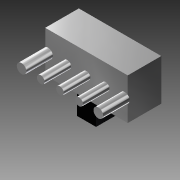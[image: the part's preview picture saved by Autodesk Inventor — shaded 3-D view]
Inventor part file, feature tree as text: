
AUTODESK INVENTOR PART (.ipt)
format: ipt  version: 2016 (Build 200138000, 138)  size: 118,272 bytes
history: native  units: mm
features: extrude x3, sketch x3, plane x1
ambient origin geometry x8: Origin, YZ Plane, XZ Plane, XY Plane, X Axis, Y Axis, Z Axis, Center Point
bodies: Solid1 (feature_tree)
feature tree (7):
  extrude  "Extrusion1"  Depth=4.3mm
  extrude  "Extrusion2"  Depth=3.5mm
  plane  "Work Plane1"
  extrude  "Extrusion3"  Depth=2.0mm
  sketch  "Sketch1"  dims[d0=8.6mm d1=4.3mm]
  sketch  "Sketch2"  dims[d2=3.5mm d3=0.0mm d4=0.8mm]
  sketch  "Sketch3"  dims[d5=0.8mm d6=0.8mm d7=2.0mm d8=2.0mm d9=1.0mm d10=1.0mm d11=2.0mm d12=2.0mm d13=2.77mm d14=0.0mm d15=-2.0mm d16=2.0mm d17=0.0mm d18=0.0mm d19=3.0mm d20=2.0mm d21=0.0mm]
